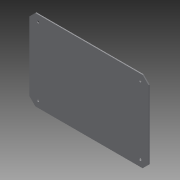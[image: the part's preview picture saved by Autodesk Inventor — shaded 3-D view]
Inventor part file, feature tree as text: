
AUTODESK INVENTOR PART (.ipt)
format: ipt  version: 2014 (Build 180170000, 170)  size: 405,504 bytes
history: native  units: mm
features: extrude x3, sketch x3, chamfer x1, other x1
ambient origin geometry x8: Origin, YZ Plane, XZ Plane, XY Plane, X Axis, Y Axis, Z Axis, Center Point
bodies: Solid1 (feature_tree)
feature tree (8):
  extrude  "Extrusion1"  Depth=95.0mm
  extrude  "Extrusion2"  Depth=1.2mm TaperAngle=0.0deg
  extrude  "Extrusion3"  Depth=80.0mm
  chamfer  "Chamfer1"  Distance=3.0mm
  sketch  "Sketch1"  dims[d0=140.0mm d1=95.0mm]
  sketch  "Sketch2"  dims[d2=1.2mm d3=0.0mm d37=1.2mm d38=0.0mm]
  other  "Image2"
  sketch  "Sketch3"  dims[d40=120.0mm d41=80.0mm d42=3.0mm d43=3.0mm d44=3.0mm d45=17.05mm d46=0.0mm d47=7.0mm d48=2.0mm d49=45.0deg]
